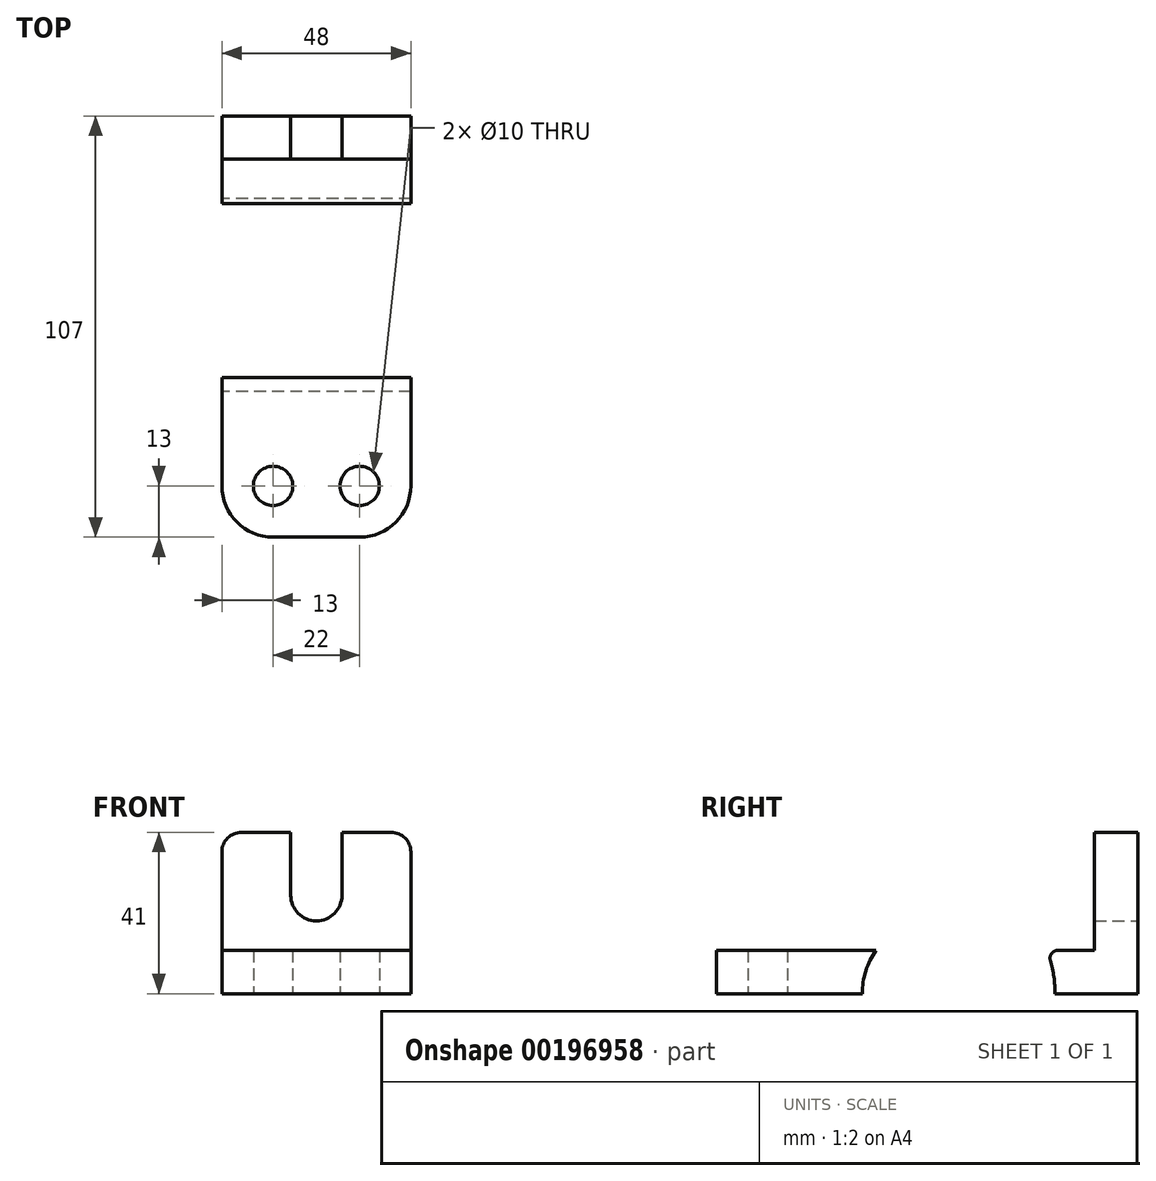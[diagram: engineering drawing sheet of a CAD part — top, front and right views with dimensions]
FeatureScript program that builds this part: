
annotation { "Feature Type Name" : "Feature", "Feature Type Description" : "" }
export const myFeature = defineFeature(function(context is Context, id is Id, definition is map)
    precondition{}
    {
        {
            var Q0;
            Q0=qCreatedBy(makeId("Right.planeOp"),FACE);
            var sketch = newSketch(context, id + "F0", { "sketchPlane" : qUnion([Q0])});
            skLineSegment(sketch, "E0.bottom", {"start": v(-53.5, 41) * mm, "end": v(53.5, 41) * mm});
            skLineSegment(sketch, "E0.top", {"start": v(-53.5, 0) * mm, "end": v(53.5, 0) * mm});
            skLineSegment(sketch, "E0.left", {"start": v(-53.5, 41) * mm, "end": v(-53.5, 0) * mm});
            skLineSegment(sketch, "E0.right", {"start": v(53.5, 41) * mm, "end": v(53.5, 0) * mm});
            skCircle(sketch, "E1", {"center": v(2.5, 0) * mm, "radius": 19 * mm});
            skCircle(sketch, "E2", {"center": v(2.5, 0) * mm, "radius": 30 * mm});
            skLineSegment(sketch, "E3", {"start": v(-53.5, 11) * mm, "end": v(42.5, 11) * mm});
            skLineSegment(sketch, "E4", {"start": v(42.5, 11) * mm, "end": v(42.5, 41) * mm});
            skSolve(sketch);
        }
        {
            var Q0;
            {var subQ0=sQuery(id+"F0.wireOp",EDGE,"E0.left");var subQ1=sQuery(id+"F0.wireOp",EDGE,"E0.top");var subQ2=makeQuery(id+"F0.imprint","INTERSECT",VERTEX,{"derivedFrom":[subQ1,subQ0]});Q0=makeQuery(id+"F0.imprint","IMPRINT",FACE,{"disambiguationData":[TD([[makeQuery(id+"F0.imprint","IMPRINT",EDGE,{"disambiguationData":[TD([[subQ2,-1.0]])],"derivedFrom":subQ1}),1.0]])]});}
            var Q1;
            {var subQ0=sQuery(id+"F0.wireOp",EDGE,"E2");var subQ1=sQuery(id+"F0.wireOp",EDGE,"E0.top");var subQ2=makeQuery(id+"F0.imprint","INTERSECT",VERTEX,{"disambiguationData":[OD(0.0)],"derivedFrom":[subQ1,subQ0]});Q1=makeQuery(id+"F0.imprint","IMPRINT",FACE,{"disambiguationData":[TD([[makeQuery(id+"F0.imprint","IMPRINT",EDGE,{"disambiguationData":[TD([[subQ2,-1.0]])],"derivedFrom":subQ1}),1.0]])]});}
            var Q2;
            {var subQ0=sQuery(id+"F0.wireOp",EDGE,"E3");var subQ1=sQuery(id+"F0.wireOp",EDGE,"E1");var subQ2=makeQuery(id+"F0.imprint","INTERSECT",VERTEX,{"disambiguationData":[OD(0.0)],"derivedFrom":[subQ1,subQ0]});Q2=makeQuery(id+"F0.imprint","IMPRINT",FACE,{"disambiguationData":[TD([[makeQuery(id+"F0.imprint","IMPRINT",EDGE,{"disambiguationData":[TD([[subQ2,-1.0]])],"derivedFrom":subQ1}),-1.0]])]});}
            var Q3;
            {var subQ0=sQuery(id+"F0.wireOp",EDGE,"E2");var subQ1=sQuery(id+"F0.wireOp",EDGE,"E0.top");var subQ2=makeQuery(id+"F0.imprint","INTERSECT",VERTEX,{"disambiguationData":[OD(1.0)],"derivedFrom":[subQ1,subQ0]});Q3=makeQuery(id+"F0.imprint","IMPRINT",FACE,{"disambiguationData":[TD([[makeQuery(id+"F0.imprint","IMPRINT",EDGE,{"disambiguationData":[TD([[subQ2,1.0]])],"derivedFrom":subQ1}),1.0]])]});}
            var Q4;
            {var subQ5=sQuery(id+"F0.wireOp",EDGE,"E0.right");Q4=makeQuery(id+"F0.imprint","IMPRINT",FACE,{"disambiguationData":[TD([[makeQuery(id+"F0.imprint","IMPRINT",EDGE,{"derivedFrom":subQ5}),-1.0]])]});}
            extrude(context, id + "F1", {"entities" : qUnion([Q0, Q1, Q2, Q3, Q4]), "endBound" : BoundingType.SYMMETRIC, "depth" : 48 * mm});
        }
        {
            var Q0;
            Q0=makeQuery(id+"F1.opExtrude","SWEPT_FACE",FACE,{"disambiguationData":[OSD([sQuery(id+"F0.wireOp",EDGE,"E0.right")])]});
            var sketch = newSketch(context, id + "F2", { "sketchPlane" : qUnion([Q0])});
            skPoint(sketch, "E5.endSnap0", {"position": v(0, 0) * mm});
            skLineSegment(sketch, "E6.bottom", {"start": v(6.5, 25) * mm, "end": v(-6.5, 25) * mm});
            skLineSegment(sketch, "E6.top", {"start": v(6.5, 57) * mm, "end": v(-6.5, 57) * mm});
            skLineSegment(sketch, "E6.left", {"start": v(6.5, 25) * mm, "end": v(6.5, 57) * mm});
            skLineSegment(sketch, "E6.right", {"start": v(-6.5, 25) * mm, "end": v(-6.5, 57) * mm});
            skPoint(sketch, "E6.middle", {"position": v(0, 41) * mm});
            skCircle(sketch, "E7", {"center": v(0, 25) * mm, "radius": 6.5 * mm});
            skSolve(sketch);
        }
        {
            var Q0;
            {var subQ0=sQuery(id+"F2.wireOp",EDGE,"E6.top");Q0=makeQuery(id+"F2.imprint","IMPRINT",FACE,{"disambiguationData":[TD([[makeQuery(id+"F2.imprint","IMPRINT",EDGE,{"derivedFrom":subQ0}),1.0]])]});}
            var Q1;
            {var subQ0=sQuery(id+"F2.wireOp",EDGE,"E7");var subQ1=sQuery(id+"F2.wireOp",EDGE,"E6.left");var subQ2=sQuery(id+"F2.wireOp",EDGE,"E6.bottom");var subQ3=makeQuery(id+"F2.imprint","INTERSECT",VERTEX,{"derivedFrom":[subQ2,subQ1,subQ0]});Q1=makeQuery(id+"F2.imprint","IMPRINT",FACE,{"disambiguationData":[TD([[makeQuery(id+"F2.imprint","IMPRINT",EDGE,{"disambiguationData":[TD([[subQ3,-1.0]])],"derivedFrom":subQ1}),1.0]])]});}
            var Q2;
            {var subQ0=sQuery(id+"F2.wireOp",EDGE,"E6.bottom");Q2=makeQuery(id+"F2.imprint","IMPRINT",FACE,{"disambiguationData":[TD([[makeQuery(id+"F2.imprint","IMPRINT",EDGE,{"derivedFrom":subQ0}),-1.0]])]});}
            var Q3;
            {var subQ0=sQuery(id+"F2.wireOp",EDGE,"E6.bottom");Q3=makeQuery(id+"F2.imprint","IMPRINT",FACE,{"disambiguationData":[TD([[makeQuery(id+"F2.imprint","IMPRINT",EDGE,{"derivedFrom":subQ0}),1.0]])]});}
            var Q4;
            Q4=makeQuery(id+"F1.opExtrude","SWEPT_FACE",FACE,{"disambiguationData":[OSD([sQuery(id+"F0.wireOp",EDGE,"E4")])]});
            extrude(context, id + "F3", {"entities" : qUnion([Q0, Q1, Q2, Q3]), "operationType" : NewBodyOperationType.REMOVE, "endBound" : BoundingType.UP_TO_SURFACE, "oppositeDirection" : true, "endBoundEntityFace" : qUnion([Q4]), "depth" : 25 * mm});
        }
        {
            var Q0;
            Q0=qCreatedBy(makeId("Top.planeOp"),FACE);
            var sketch = newSketch(context, id + "F4", { "sketchPlane" : qUnion([Q0])});
            skCircle(sketch, "E8", {"center": v(-11, -40.5) * mm, "radius": 5 * mm});
            skCircle(sketch, "E9", {"center": v(11, -40.5) * mm, "radius": 5 * mm});
            skCircle(sketch, "E10", {"center": v(-11, -40.5) * mm, "radius": 13 * mm, "construction": true});
            skCircle(sketch, "E11", {"center": v(0, 2.5) * mm, "radius": 2.5 * mm});
            skSolve(sketch);
        }
        {
            var Q0;
            Q0 = qSketchRegion(id + "F4", true);
            extrude(context, id + "F5", {"entities" : qUnion([Q0]), "operationType" : NewBodyOperationType.REMOVE, "endBound" : BoundingType.THROUGH_ALL, "depth" : 25 * mm});
        }
        {
            var Q0;
            Q0=makeQuery(id+"F1.opExtrude","CAP_EDGE",EDGE,{"disambiguationData":[OSD([sQuery(id+"F0.wireOp",EDGE,"E0.bottom")])],"isStart":true});
            var Q1;
            Q1=makeQuery(id+"F1.opExtrude","CAP_EDGE",EDGE,{"disambiguationData":[OSD([sQuery(id+"F0.wireOp",EDGE,"E0.bottom")])],"isStart":false});
            fillet(context, id + "F6", {"entities" : qUnion([Q0, Q1]), "radius" : 5 * mm, "tangentPropagation" : true, "allowEdgeOverflow" : false});
        }
        {
            var Q0;
            Q0=makeQuery(id+"F1.opExtrude","CAP_EDGE",EDGE,{"disambiguationData":[OSD([sQuery(id+"F0.wireOp",EDGE,"E0.left")])],"isStart":true});
            var Q1;
            Q1=makeQuery(id+"F1.opExtrude","CAP_EDGE",EDGE,{"disambiguationData":[OSD([sQuery(id+"F0.wireOp",EDGE,"E0.left")])],"isStart":false});
            fillet(context, id + "F7", {"entities" : qUnion([Q0, Q1]), "radius" : 13 * mm, "tangentPropagation" : true, "allowEdgeOverflow" : false});
        }
        {
            var Q0;
            {var subQ0=sQuery(id+"F0.wireOp",EDGE,"E3");var subQ1=sQuery(id+"F0.wireOp",EDGE,"E2");Q0=makeQuery(id+"F1.opExtrude","SWEPT_EDGE",EDGE,{"disambiguationData":[OSD([subQ1,subQ0]),TDD([makeQuery(id+"F0.imprint","INTERSECT",VERTEX,{"disambiguationData":[OD(1.0)],"derivedFrom":[subQ1,subQ0]})])]});}
            var Q1;
            {var subQ0=sQuery(id+"F0.wireOp",EDGE,"E3");var subQ1=sQuery(id+"F0.wireOp",EDGE,"E2");Q1=makeQuery(id+"F1.opExtrude","SWEPT_EDGE",EDGE,{"disambiguationData":[OSD([subQ1,subQ0]),TDD([makeQuery(id+"F0.imprint","INTERSECT",VERTEX,{"disambiguationData":[OD(0.0)],"derivedFrom":[subQ1,subQ0]})])]});}
            fillet(context, id + "F8", {"entities" : qUnion([Q0, Q1]), "radius" : 2 * mm, "tangentPropagation" : true, "allowEdgeOverflow" : false});
        }
    });
